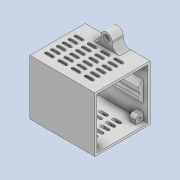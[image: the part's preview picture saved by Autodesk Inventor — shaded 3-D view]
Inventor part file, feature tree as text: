
AUTODESK INVENTOR PART (.ipt)
format: ipt  version: 2021 (Build 250183000, 183)  size: 543,744 bytes
history: native  units: mm
features: sketch x8, extrude x8, projected_geometry x5, plane x3, mirror x2, pattern_linear x1, fillet x1, hole x1
ambient origin geometry x8: Origin, YZ Plane, XZ Plane, XY Plane, X Axis, Y Axis, Z Axis, Center Point
bodies: Solid1 (feature_tree)
feature tree (29):
  sketch  "Sketch1"  dims[d0=75.0mm d1=75.0mm]
  extrude  "Extrusion1"  Depth=75.0mm
  extrude  "Extrusion2"  TaperAngle=45.0deg  [1 undecoded]
  sketch  "Sketch3"  dims[d2=3.0mm d4=45.0deg]
  plane  "Work Plane1"
  extrude  "Extrusion3"  Depth=60.5mm
  pattern_linear  "Rectangular Pattern1"  Spacing1=3.0mm  [1 undecoded]
  mirror  "Mirror1"
  extrude  "Extrusion4"  Depth=42.5mm
  plane  "Work Plane2"
  sketch  "Sketch7"  dims[d8=56.0mm]
  extrude  "Extrusion5"  [1 undecoded]
  extrude  "Extrusion6"  Depth=4.0mm
  plane  "Work Plane3"
  extrude  "Extrusion8"  Depth=5.0mm
  extrude  "Extrusion10"  Depth=8.0mm TaperAngle=0.0deg
  fillet  "Fillet3"  Radius=60.0mm
  hole  "Hole2"  [1 undecoded]
  mirror  "Mirror6"
  sketch  "Sketch5"  dims[d5=60.5mm d6=1.8mm]
  sketch  "Sketch6"  dims[d7=1.8mm]
  projected_geometry  "Projected Loop1"
  projected_geometry  "Projected Loop2"
  sketch  "Sketch8"  dims[d9=15.0mm]
  projected_geometry  "Projected Loop3"
  sketch  "Sketch12"  dims[d10=15.0mm]
  projected_geometry  "Projected Loop6"
  sketch  "Sketch13"  dims[d11=85.0mm d12=0.0mm d13=3.0mm d14=0.0mm d16=42.5mm d17=-7.853982mm d19=4.0mm d20=5.0mm d21=33.0mm d22=0.0mm d23=60.0mm d25=8.0mm d26=40.0mm d28=18.0mm d30=33.0mm d31=0.0mm d32=-6.5mm d33=4.3mm d34=5.0mm d35=5.0mm d36=7.2mm d37=8.0mm d38=0.0mm d39=4.0mm d40=0.0mm d41=5.0mm d42=5.0mm d43=7.2mm d44=4.3mm d48=3.0mm d49=3.0mm d50=3.0mm d51=4.0mm d52=0.0mm d80=15.0mm d81=12.0mm d82=15.0mm d83=0.0mm d84=10.0mm d85=9.0mm d86=6.0mm d87=15.0mm d88=9.0mm d89=90.0deg d90=8.0mm d91=20.594885mm d61=0.5mm d62=0.872665mm d63=0.5mm d64=0.872665mm]
  projected_geometry  "Projected Loop7"
note: 4 required parameter values undecoded (feature->parameter linkage not recoverable at this tier; creation-order binding heuristic only, values carry confidence <= 0.55)
